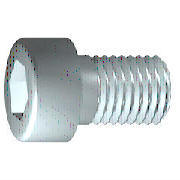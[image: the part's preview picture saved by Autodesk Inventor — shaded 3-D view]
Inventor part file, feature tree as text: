
AUTODESK INVENTOR PART (.ipt)
format: ipt  version: 2018 (Build 220112000, 112)  size: 183,808 bytes
history: native  units: mm (DEFAULTED — no unit token found)
features: sketch x2, extrude x1, plane x1, fillet x1
ambient origin geometry x7: Origin, YZ Plane, XY Plane, X Axis, Y Axis, Z Axis, Center Point
bodies: Solid1 (feature_tree), Body (feature_tree)
feature tree (5):
  extrude  "Slot"  Depth=3.0mm
  plane  "Work Plane1"
  fillet  "Fillet2"  Radius=3.0mm
  sketch  "Sketch1"  dims[d1=18.0mm d2=0.306825mm d3=3.0mm]
  sketch  "Sketch2"  dims[d4=1.5mm d5=60.0deg d6=3.0mm d7=3.0mm d8=2.886751mm d9=5.5mm d10=90.0deg d11=10.0mm d12=0.0mm d13=18.0mm d14=0.0mm d15=0.306725mm d16=0.306725mm d17=0.3mm d19=0.0mm d26=30.0mm d27=45.0deg d28=0.0mm d29=0.0mm d30=0.1mm]
